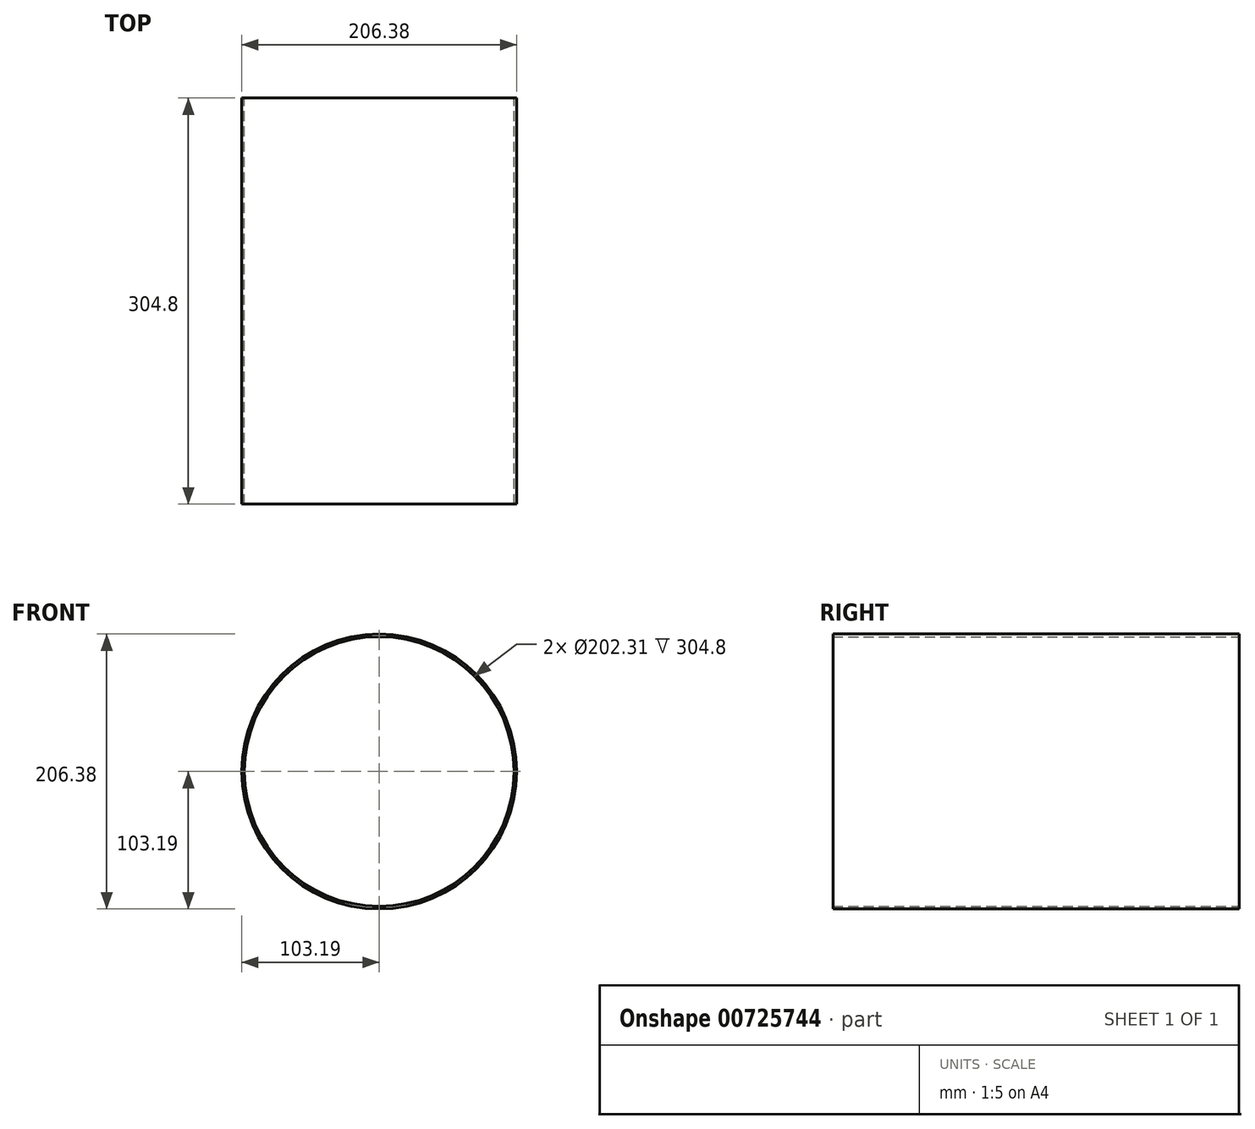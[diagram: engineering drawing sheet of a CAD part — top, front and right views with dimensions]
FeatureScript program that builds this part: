
annotation { "Feature Type Name" : "Feature", "Feature Type Description" : "" }
export const myFeature = defineFeature(function(context is Context, id is Id, definition is map)
    precondition{}
    {
        {
            var Q0;
            Q0=qCreatedBy(makeId("Front.planeOp"),FACE);
            var sketch = newSketch(context, id + "F0", { "sketchPlane" : qUnion([Q0])});
            skCircle(sketch, "E0", {"center": v(0, 0) * mm, "radius": 101.16 * mm});
            skCircle(sketch, "E1", {"center": v(0, 0) * mm, "radius": 103.19 * mm});
            skSolve(sketch);
        }
        {
            var Q0;
            Q0 = qSketchRegion(id + "F0", true);
            extrude(context, id + "F1", {"entities" : qUnion([Q0]), "depth" : 304.8 * mm, "offsetDistance" : 25.4 * mm});
        }
    });
